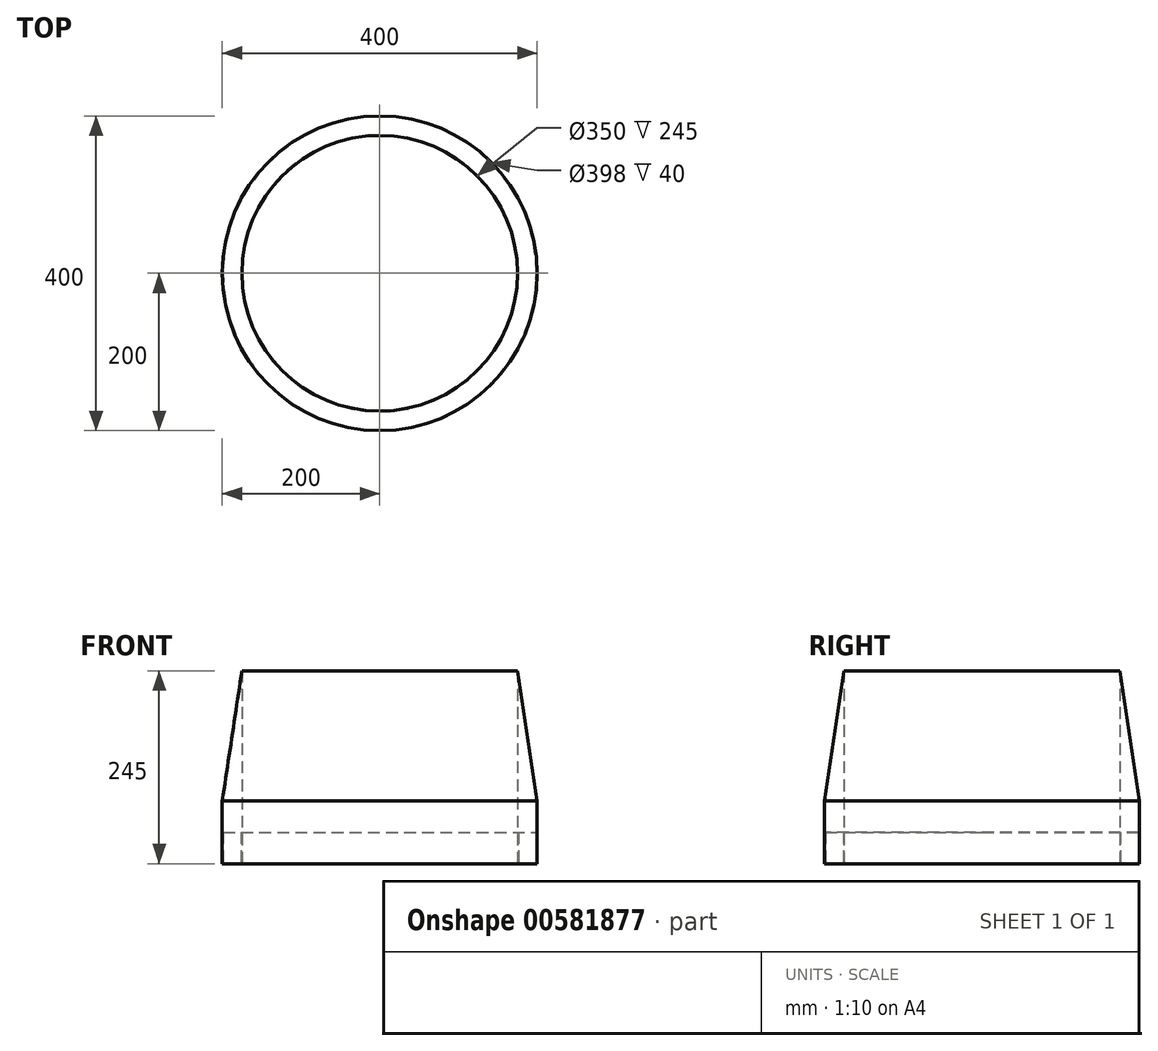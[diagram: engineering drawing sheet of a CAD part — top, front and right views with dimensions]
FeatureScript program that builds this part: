
annotation { "Feature Type Name" : "Feature", "Feature Type Description" : "" }
export const myFeature = defineFeature(function(context is Context, id is Id, definition is map)
    precondition{}
    {
        {
            var Q0;
            Q0=qCreatedBy(makeId("Front.planeOp"),FACE);
            var sketch = newSketch(context, id + "F0", { "sketchPlane" : qUnion([Q0])});
            skLineSegment(sketch, "E0", {"start": v(0, -139.25) * mm, "end": v(0, 240.83) * mm, "construction": true});
            skLineSegment(sketch, "E1", {"start": v(-175, -67.22) * mm, "end": v(-175, 177.78) * mm});
            skLineSegment(sketch, "E2", {"start": v(-175, 177.78) * mm, "end": v(-200, 12.78) * mm});
            skLineSegment(sketch, "E3", {"start": v(-200, 12.78) * mm, "end": v(-200, -67.22) * mm});
            skLineSegment(sketch, "E4", {"start": v(-200, -67.22) * mm, "end": v(-199, -67.22) * mm});
            skLineSegment(sketch, "E5", {"start": v(-199, -67.22) * mm, "end": v(-199, -27.22) * mm});
            skLineSegment(sketch, "E6", {"start": v(-199, -27.22) * mm, "end": v(-176, -27.22) * mm});
            skLineSegment(sketch, "E7", {"start": v(-176, -27.22) * mm, "end": v(-176, -67.22) * mm});
            skLineSegment(sketch, "E8", {"start": v(-176, -67.22) * mm, "end": v(-175, -67.22) * mm});
            skSolve(sketch);
        }
        {
            var Q0;
            Q0=qSketchRegion(id+"F0",true);
            var Q1;
            Q1=sQuery(id+"F0.wireOp",EDGE,"E0");
            revolve(context, id + "F1", {"entities" : qUnion([Q0]), "axis" : qUnion([Q1]), "revolveType" : RevolveType.FULL});
        }
    });
